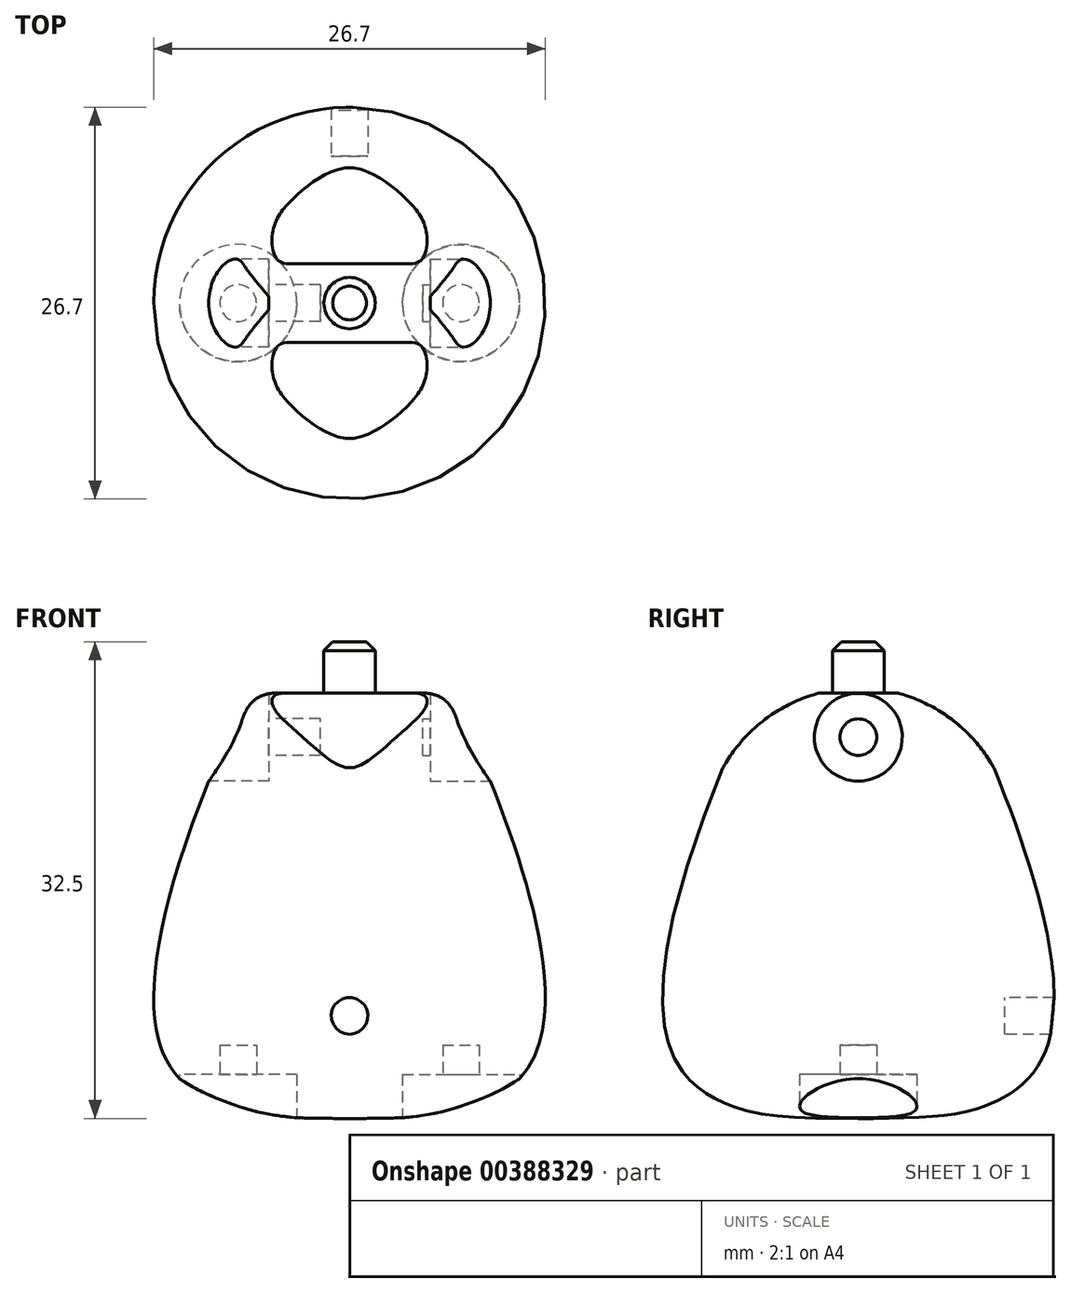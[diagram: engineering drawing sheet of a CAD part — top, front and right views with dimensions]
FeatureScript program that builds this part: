
annotation { "Feature Type Name" : "Feature", "Feature Type Description" : "" }
export const myFeature = defineFeature(function(context is Context, id is Id, definition is map)
    precondition{}
    {
        {
            var Q0;
            Q0=qCreatedBy(makeId("Front.planeOp"),FACE);
            cPlane(context, id + "F0", {"entities" : qUnion([Q0]), "cplaneType" : CPlaneType.OFFSET, "offset" : 10 * mm, "oppositeDirection" : true, "width" : 150 * mm, "height" : 150 * mm});
        }
        {
            var Q0;
            Q0=qCreatedBy(makeId("Front.planeOp"),FACE);
            var sketch = newSketch(context, id + "F1", { "sketchPlane" : qUnion([Q0])});
            skLineSegment(sketch, "E0", {"start": v(-7, 29) * mm, "end": v(0, 29) * mm});
            skLineSegment(sketch, "E1", {"start": v(0, 29) * mm, "end": v(0, 0) * mm});
            skFitSpline(sketch, "E2", {"points": [v(0, 0) * mm, v(-9, 1) * mm, v(-12.5, 4) * mm, v(-7, 29) * mm], "startDerivative": vector(-54.16, 0) * mm, "endDerivative": vector(38.26, 82.57) * mm});
            skLineSegment(sketch, "E3", {"start": v(0, 75.02) * mm, "end": v(0, -60.78) * mm, "construction": true});
            skSolve(sketch);
        }
        {
            var Q0;
            Q0 = qSketchRegion(id + "F1", true);
            var Q1;
            Q1=sQuery(id+"F1.wireOp",EDGE,"E3");
            revolve(context, id + "F2", {"entities" : qUnion([Q0]), "axis" : qUnion([Q1]), "revolveType" : RevolveType.FULL});
        }
        {
            var Q0;
            Q0=qCreatedBy(makeId("Top.planeOp"),FACE);
            var sketch = newSketch(context, id + "F3", { "sketchPlane" : qUnion([Q0])});
            skCircle(sketch, "E4", {"center": v(-7.6, 0) * mm, "radius": 4 * mm});
            skCircle(sketch, "E5", {"center": v(7.6, 0) * mm, "radius": 4 * mm});
            skSolve(sketch);
        }
        {
            var Q0;
            Q0 = qSketchRegion(id + "F3", true);
            extrude(context, id + "F4", {"entities" : qUnion([Q0]), "operationType" : NewBodyOperationType.REMOVE, "depth" : 3 * mm});
        }
        {
            var Q0;
            Q0=makeQuery(id+"F4.boolean.opBoolean","COPY",FACE,{"derivedFrom":makeQuery(id+"F4.opExtrude","CAP_FACE",FACE,{"disambiguationData":[OSD([sQuery(id+"F3.wireOp",EDGE,"E5")])],"isStart":false})});
            var sketch = newSketch(context, id + "F5", { "sketchPlane" : qUnion([Q0])});
            skCircle(sketch, "E6", {"center": v(7.6, 0) * mm, "radius": 1.25 * mm});
            skSolve(sketch);
        }
        {
            var Q0;
            Q0 = qSketchRegion(id + "F5", true);
            extrude(context, id + "F6", {"entities" : qUnion([Q0]), "operationType" : NewBodyOperationType.REMOVE, "oppositeDirection" : true, "depth" : 2 * mm});
        }
        {
            var Q0;
            Q0=makeQuery(id+"F4.boolean.opBoolean","COPY",FACE,{"derivedFrom":makeQuery(id+"F4.opExtrude","CAP_FACE",FACE,{"disambiguationData":[OSD([sQuery(id+"F3.wireOp",EDGE,"E4")])],"isStart":false})});
            var sketch = newSketch(context, id + "F7", { "sketchPlane" : qUnion([Q0])});
            skCircle(sketch, "E7", {"center": v(-7.6, 0) * mm, "radius": 1.25 * mm});
            skSolve(sketch);
        }
        {
            var Q0;
            Q0 = qSketchRegion(id + "F7", true);
            extrude(context, id + "F8", {"entities" : qUnion([Q0]), "operationType" : NewBodyOperationType.REMOVE, "oppositeDirection" : true, "depth" : 2 * mm});
        }
        {
            var Q0;
            Q0=qCreatedBy(makeId("Right.planeOp"),FACE);
            var sketch = newSketch(context, id + "F9", { "sketchPlane" : qUnion([Q0])});
            skArc(sketch, "E8", {"start": v(-10.11, 21.8) * mm, "mid": v(0, 29.35) * mm, "end": v(10.11, 21.8) * mm});
            skLineSegment(sketch, "E9", {"start": v(0, 47.28) * mm, "end": v(0, -3.34) * mm, "construction": true});
            skLineSegment(sketch, "E10", {"start": v(-10.11, 21.8) * mm, "end": v(-10.11, 31.8) * mm});
            skLineSegment(sketch, "E11", {"start": v(-10.11, 31.8) * mm, "end": v(10.11, 31.8) * mm});
            skLineSegment(sketch, "E12", {"start": v(10.11, 31.8) * mm, "end": v(10.11, 21.8) * mm});
            skSolve(sketch);
        }
        {
            var Q0;
            Q0 = qSketchRegion(id + "F9", true);
            extrude(context, id + "F10", {"entities" : qUnion([Q0]), "operationType" : NewBodyOperationType.REMOVE, "endBound" : BoundingType.SYMMETRIC, "oppositeDirection" : true, "depth" : 25 * mm});
        }
        {
            var Q0;
            Q0=makeQuery(id+"F10.boolean.opBoolean","SPLIT",EDGE,{"disambiguationData":[OD(1.0)],"derivedFrom":makeQuery(id+"F2.opRevolve","SWEPT_EDGE",EDGE,{"disambiguationData":[OSD([sQuery(id+"F1.wireOp",EDGE,"E0"),sQuery(id+"F1.wireOp",EDGE,"E2")])]})});
            var Q1;
            Q1=makeQuery(id+"F10.boolean.opBoolean","SPLIT",EDGE,{"disambiguationData":[OD(0.0)],"derivedFrom":makeQuery(id+"F2.opRevolve","SWEPT_EDGE",EDGE,{"disambiguationData":[OSD([sQuery(id+"F1.wireOp",EDGE,"E0"),sQuery(id+"F1.wireOp",EDGE,"E2")])]})});
            fillet(context, id + "F11", {"entities" : qUnion([Q0, Q1]), "radius" : 3 * mm, "tangentPropagation" : true, "allowEdgeOverflow" : false});
        }
        {
            var Q0;
            Q0=makeQuery(id+"F2.opRevolve","SWEPT_FACE",FACE,{"disambiguationData":[OSD([sQuery(id+"F1.wireOp",EDGE,"E0")])]});
            var sketch = newSketch(context, id + "F12", { "sketchPlane" : qUnion([Q0])});
            skCircle(sketch, "E13", {"center": v(0, 0) * mm, "radius": 1.75 * mm});
            skSolve(sketch);
        }
        {
            var Q0;
            Q0 = qSketchRegion(id + "F12", true);
            extrude(context, id + "F13", {"entities" : qUnion([Q0]), "operationType" : NewBodyOperationType.ADD, "depth" : 3.5 * mm});
        }
        {
            var Q0;
            Q0=makeQuery(id+"F13.opExtrude","CAP_EDGE",EDGE,{"disambiguationData":[OSD([sQuery(id+"F12.wireOp",EDGE,"E13")])],"isStart":false});
            chamfer(context, id + "F14", {"entities" : qUnion([Q0]), "width" : 0.6 * mm, "tangentPropagation" : true});
        }
        {
            var Q0;
            Q0=qCreatedBy(id+"F0.planeOp",FACE);
            var sketch = newSketch(context, id + "F15", { "sketchPlane" : qUnion([Q0])});
            skCircle(sketch, "E14", {"center": v(0, 7) * mm, "radius": 1.25 * mm});
            skSolve(sketch);
        }
        {
            var Q0;
            Q0 = qSketchRegion(id + "F15", true);
            extrude(context, id + "F16", {"entities" : qUnion([Q0]), "operationType" : NewBodyOperationType.REMOVE, "endBound" : BoundingType.UP_TO_NEXT, "oppositeDirection" : true, "depth" : 25 * mm});
        }
        {
            var Q0;
            Q0=qCreatedBy(makeId("Right.planeOp"),FACE);
            cPlane(context, id + "F17", {"entities" : qUnion([Q0]), "cplaneType" : CPlaneType.OFFSET, "offset" : 10 * mm, "width" : 150 * mm, "height" : 150 * mm});
        }
        {
            var Q0;
            Q0=qCreatedBy(makeId("Right.planeOp"),FACE);
            cPlane(context, id + "F18", {"entities" : qUnion([Q0]), "cplaneType" : CPlaneType.OFFSET, "offset" : 10 * mm, "oppositeDirection" : true, "width" : 150 * mm, "height" : 150 * mm});
        }
        {
            var Q0;
            Q0=qCreatedBy(id+"F17.planeOp",FACE);
            var sketch = newSketch(context, id + "F19", { "sketchPlane" : qUnion([Q0])});
            skCircle(sketch, "E15", {"center": v(0, 26) * mm, "radius": 1.25 * mm});
            skSolve(sketch);
        }
        {
            var Q0;
            Q0 = qSketchRegion(id + "F19", true);
            extrude(context, id + "F20", {"entities" : qUnion([Q0]), "operationType" : NewBodyOperationType.REMOVE, "oppositeDirection" : true, "depth" : 5 * mm});
        }
        {
            var Q0;
            Q0=qCreatedBy(id+"F17.planeOp",FACE);
            var sketch = newSketch(context, id + "F21", { "sketchPlane" : qUnion([Q0])});
            skCircle(sketch, "E16", {"center": v(0, 26) * mm, "radius": 3 * mm});
            skSolve(sketch);
        }
        {
            var Q0;
            Q0 = qSketchRegion(id + "F21", true);
            extrude(context, id + "F22", {"entities" : qUnion([Q0]), "operationType" : NewBodyOperationType.REMOVE, "oppositeDirection" : true, "depth" : 4.5 * mm});
        }
        {
            var Q0;
            Q0=qCreatedBy(id+"F18.planeOp",FACE);
            var sketch = newSketch(context, id + "F23", { "sketchPlane" : qUnion([Q0])});
            skCircle(sketch, "E17", {"center": v(0, 26) * mm, "radius": 1.25 * mm});
            skSolve(sketch);
        }
        {
            var Q0;
            Q0 = qSketchRegion(id + "F23", true);
            extrude(context, id + "F24", {"entities" : qUnion([Q0]), "operationType" : NewBodyOperationType.REMOVE, "depth" : 8 * mm});
        }
        {
            var Q0;
            Q0=qCreatedBy(id+"F18.planeOp",FACE);
            var sketch = newSketch(context, id + "F25", { "sketchPlane" : qUnion([Q0])});
            skCircle(sketch, "E18", {"center": v(0, 26) * mm, "radius": 3 * mm});
            skSolve(sketch);
        }
        {
            var Q0;
            Q0 = qSketchRegion(id + "F25", true);
            extrude(context, id + "F26", {"entities" : qUnion([Q0]), "operationType" : NewBodyOperationType.REMOVE, "depth" : 4.5 * mm});
        }
    });
